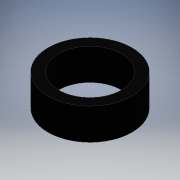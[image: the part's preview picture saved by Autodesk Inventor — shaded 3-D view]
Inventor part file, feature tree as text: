
AUTODESK INVENTOR PART (.ipt)
format: ipt  version: 2016 (Build 200138000, 138)  size: 93,184 bytes
history: native  units: mm
features: other x1, extrude x1, sketch x1
ambient origin geometry x8: Origin, YZ Plane, XZ Plane, XY Plane, X Axis, Y Axis, Z Axis, Center Point
bodies: Body1 (feature_tree)
feature tree (3):
  other  "ソリッド1"
  extrude  "押し出し1"  Depth=8.0mm
  sketch  "スケッチ1"
